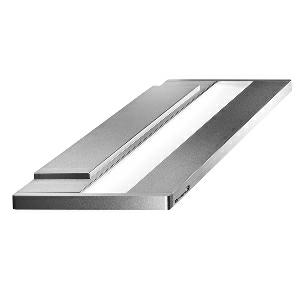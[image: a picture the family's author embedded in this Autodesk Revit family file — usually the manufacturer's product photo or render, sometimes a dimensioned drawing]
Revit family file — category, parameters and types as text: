
# Revit family: zera_bed_-_zew_11000_830_-_ul_li_lvc_nl_00813010_dbb4
name_source: partatom
category: Lighting Fixtures
units: mm (PartAtom-declared; Revit-internal decimal feet)

## family parameters
Cut with Voids When Loaded = No
Host = Face
Light Source = No
Part Type = Normal
Room Calculation Point = No
Round Connector Dimension = Use Diameter
Shared = No

## types (1)
- AL+UL (1 x LED, 9800 lm, 4000K/3000K)
    Apparent Load = 109 VA
    Approval mark = CE
    CIE Flux Codes = 45 81 99 47 100
    Color Rendering = 90/80
    Color Temperature = 4000K/3000K
    Default Elevation = 2000 mm  [stored 6.56168 ft]
    Description = ZERA.bed - ZEW 11000/830
    Frequency = 50 Hz, 60 Hz
    Height = 20 mm  [stored 0.0656168 ft]
    Lamp = 1 x LED
    Lamp Light Flux = 9800 lm
    Lamp count = 1
    Length = 1050 mm
    Luminous efficacy = 90 lm/W
    Manufacturer = Waldmann
    ModVariant = No
    Model = 00813010
    Mounting Place = Wall
    Mounting Type = Surface mounted
    Number of Poles = 1
    OnlyDefault = Yes
    Power Factor = 1
    Product Name = ZERA.bed - ZEW 11000/830 - UL LI/LVC/NL
    Product group = Wall mounted Luminaire
    ProductGroupID = 20
    Protection Class = Protection class I
    Protection Degree = IP 20
    RLX_Detail_Level = 1
    RLX_Emergency_Light_Flux = 0 lm
    RLX_Emergency_Type = 0
    RLX_Emergency_Type_DB = No
    RlxData = <blob elided: 60133 chars, md5=756df299>
    Socket = socket
    Standby Power = 0 W
    System Light Flux = 9800 lm
    System Power = 109 W
    Type Comments = General and Examation Light
    Type Image = zera_bed.jpg
    URL = http://relux.com
    VarID = al_ul_37f9
    Voltage = 230 V
    Voltage Range = 220-240 V
    Weight = 0.00 kg
    Width = 230 mm

note: [stored X ft] marks values corroborated as IEEE doubles in the binary element streams (Revit-internal decimal feet)

## geometry (parser evidence)
native form markers: Blend x4, Sweep x14
no freeform markers — native parametric forms only
